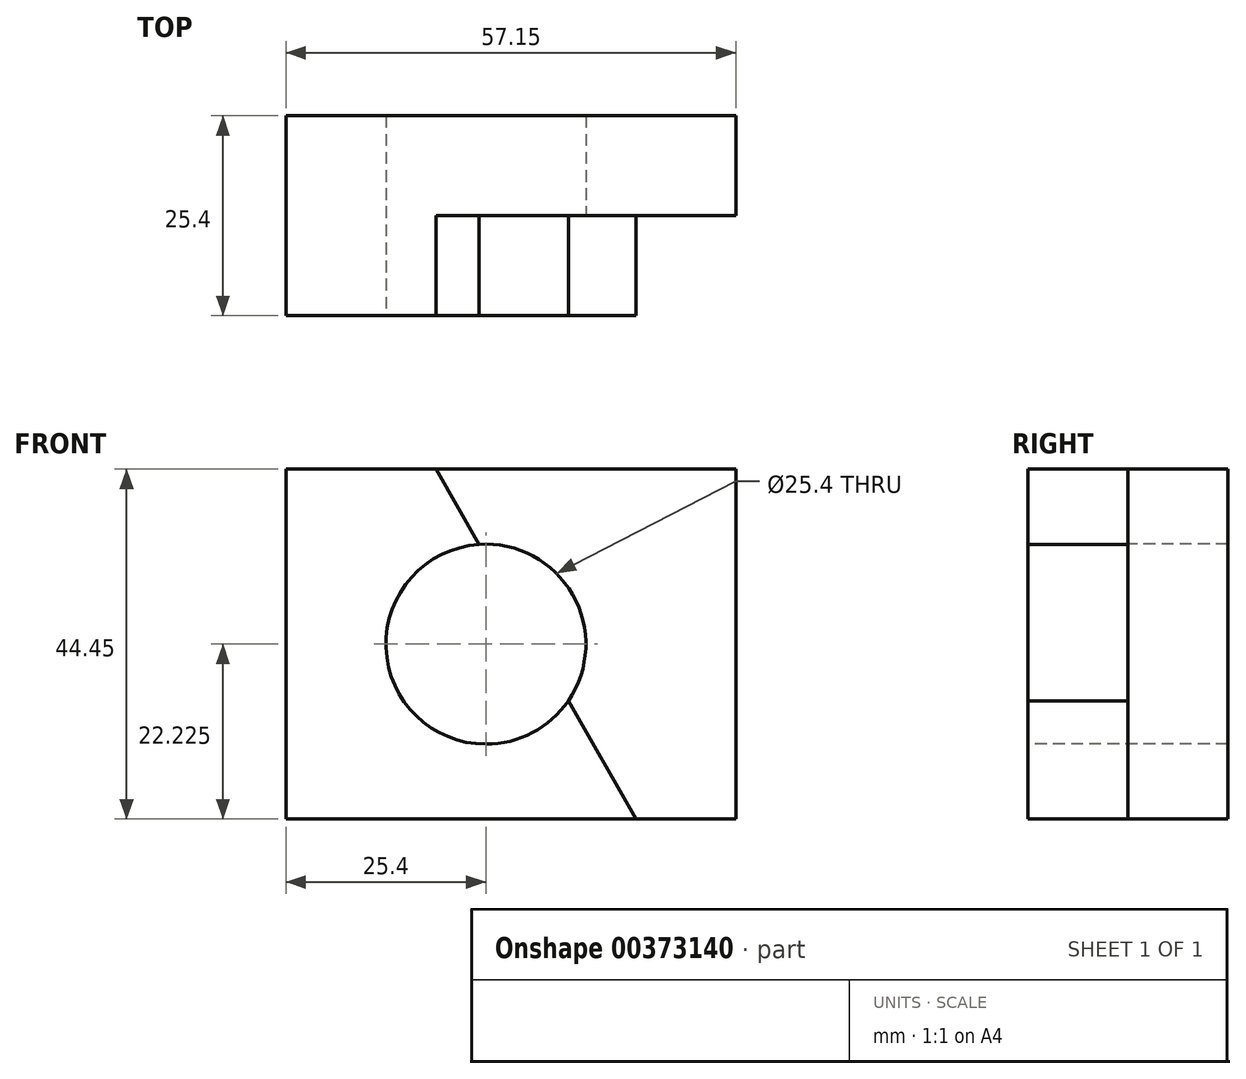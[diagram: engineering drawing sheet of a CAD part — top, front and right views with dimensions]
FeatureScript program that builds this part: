
annotation { "Feature Type Name" : "Feature", "Feature Type Description" : "" }
export const myFeature = defineFeature(function(context is Context, id is Id, definition is map)
    precondition{}
    {
        {
            var Q0;
            Q0=qCreatedBy(makeId("Front.planeOp"),FACE);
            var sketch = newSketch(context, id + "F0", { "sketchPlane" : qUnion([Q0])});
            skLineSegment(sketch, "E0", {"start": v(0, 0) * mm, "end": v(57.15, 0) * mm});
            skLineSegment(sketch, "E1", {"start": v(57.15, 0) * mm, "end": v(57.15, 44.45) * mm});
            skLineSegment(sketch, "E2", {"start": v(57.15, 44.45) * mm, "end": v(0, 44.45) * mm});
            skLineSegment(sketch, "E3", {"start": v(0, 44.45) * mm, "end": v(0, 0) * mm});
            skSolve(sketch);
        }
        {
            var Q0;
            Q0 = qSketchRegion(id + "F0", true);
            extrude(context, id + "F1", {"entities" : qUnion([Q0]), "oppositeDirection" : true, "depth" : 25.4 * mm});
        }
        {
            var Q0;
            Q0=makeQuery(id+"F1.opExtrude","CAP_FACE",FACE,{"disambiguationData":[OSD([sQuery(id+"F0.wireOp",EDGE,"E0"),sQuery(id+"F0.wireOp",EDGE,"E1"),sQuery(id+"F0.wireOp",EDGE,"E2"),sQuery(id+"F0.wireOp",EDGE,"E3")])],"isStart":true});
            var sketch = newSketch(context, id + "F2", { "sketchPlane" : qUnion([Q0])});
            skLineSegment(sketch, "E4", {"start": v(0, 22.23) * mm, "end": v(25.4, 22.23) * mm});
            skCircle(sketch, "E5", {"center": v(25.4, 22.23) * mm, "radius": 12.7 * mm});
            skSolve(sketch);
        }
        {
            var Q0;
            Q0 = qSketchRegion(id + "F2", true);
            extrude(context, id + "F3", {"entities" : qUnion([Q0]), "operationType" : NewBodyOperationType.REMOVE, "oppositeDirection" : true, "depth" : 25.4 * mm});
        }
        {
            var Q0;
            Q0=makeQuery(id+"F1.opExtrude","CAP_FACE",FACE,{"disambiguationData":[OSD([sQuery(id+"F0.wireOp",EDGE,"E0"),sQuery(id+"F0.wireOp",EDGE,"E1"),sQuery(id+"F0.wireOp",EDGE,"E2"),sQuery(id+"F0.wireOp",EDGE,"E3")])],"isStart":true});
            var sketch = newSketch(context, id + "F4", { "sketchPlane" : qUnion([Q0])});
            skLineSegment(sketch, "E6", {"start": v(0, 44.45) * mm, "end": v(19.05, 44.45) * mm});
            skLineSegment(sketch, "E7", {"start": v(19.05, 44.45) * mm, "end": v(44.45, 0) * mm});
            skLineSegment(sketch, "E8", {"start": v(44.45, 0) * mm, "end": v(57.15, 0) * mm});
            skLineSegment(sketch, "E9", {"start": v(0, 44.45) * mm, "end": v(0, 0) * mm});
            skLineSegment(sketch, "E10", {"start": v(0, 0) * mm, "end": v(44.45, 0) * mm});
            skSolve(sketch);
        }
        {
            var Q0;
            {var subQ1=sQuery(id+"F4.wireOp",EDGE,"E8");Q0=makeQuery(id+"F4.imprint","IMPRINT",FACE,{"disambiguationData":[TD([[makeQuery(id+"F4.imprint","IMPRINT",EDGE,{"derivedFrom":subQ1}),1.0]])]});}
            extrude(context, id + "F5", {"entities" : qUnion([Q0]), "operationType" : NewBodyOperationType.REMOVE, "oppositeDirection" : true, "depth" : 12.7 * mm});
        }
    });
